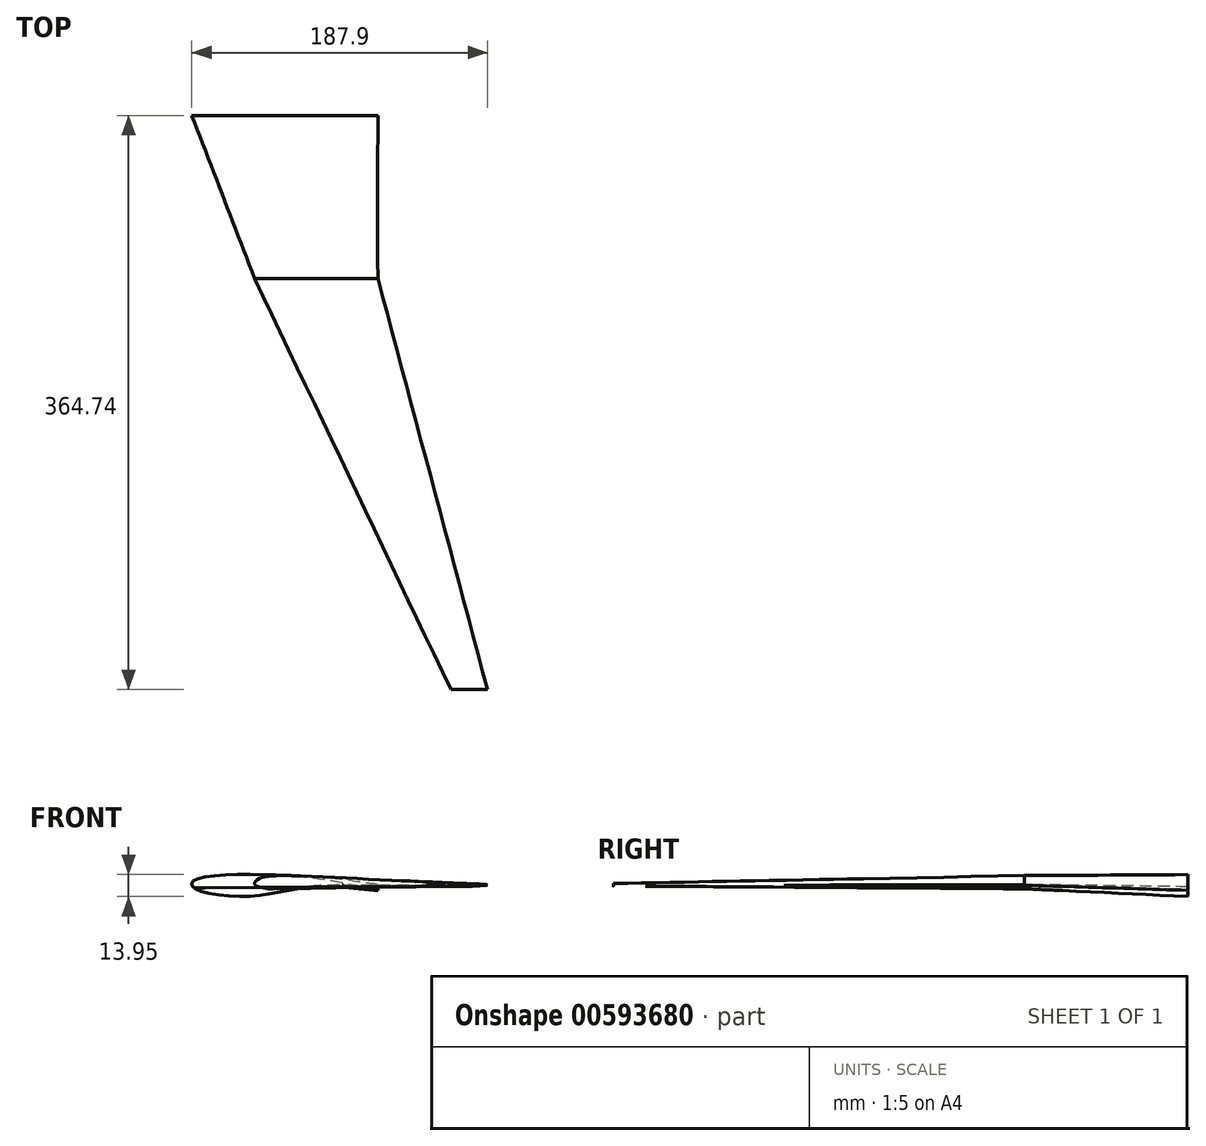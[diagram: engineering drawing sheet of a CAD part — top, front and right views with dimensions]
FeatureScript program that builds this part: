
annotation { "Feature Type Name" : "Feature", "Feature Type Description" : "" }
export const myFeature = defineFeature(function(context is Context, id is Id, definition is map)
    precondition{}
    {
        {
            var Q0;
            Q0=qCreatedBy(makeId("Front.planeOp"),FACE);
            cPlane(context, id + "F0", {"entities" : qUnion([Q0]), "cplaneType" : CPlaneType.OFFSET, "offset" : 129.03 * mm, "width" : 152.4 * mm, "height" : 152.4 * mm});
        }
        {
            var Q0;
            Q0=qCreatedBy(id+"F0.planeOp",FACE);
            var sketch = newSketch(context, id + "F1", { "sketchPlane" : qUnion([Q0])});
            skFitSpline(sketch, "E0", {"points": [v(59.9, 0) * mm, v(25.42, 4.56) * mm, v(1.57, 5.93) * mm, v(-15.04, 4.16) * mm, v(-18.32, 0.69) * mm, v(-14.73, -1.47) * mm, v(-7.44, -2.48) * mm, v(4.73, -1.57) * mm, v(25.42, 0) * mm, v(47.18, 0) * mm, v(59.9, 0) * mm]});
            skSolve(sketch);
        }
        {
            var Q0;
            Q0=qCreatedBy(makeId("Front.planeOp"),FACE);
            cPlane(context, id + "F2", {"entities" : qUnion([Q0]), "cplaneType" : CPlaneType.OFFSET, "offset" : 25.4 * mm, "width" : 152.4 * mm, "height" : 152.4 * mm});
        }
        {
            var Q0;
            Q0=qCreatedBy(id+"F2.planeOp",FACE);
            var sketch = newSketch(context, id + "F3", { "sketchPlane" : qUnion([Q0])});
            skFitSpline(sketch, "E1", {"points": [v(59.96, -3.36) * mm, v(25.15, 3.2) * mm, v(-14.76, 6.49) * mm, v(-55.04, 3.75) * mm, v(-58.32, 0.28) * mm, v(-55.04, -3) * mm, v(-24.6, -7.37) * mm, v(5.1, -3.17) * mm, v(25.34, -1.17) * mm, v(47.02, -2.26) * mm, v(59.96, -3.36) * mm]});
            skSolve(sketch);
        }
        {
            var Q0;
            Q0=qCreatedBy(id+"F0.planeOp",FACE);
            cPlane(context, id + "F4", {"entities" : qUnion([Q0]), "cplaneType" : CPlaneType.OFFSET, "offset" : 261.1 * mm, "width" : 152.4 * mm, "height" : 152.4 * mm});
        }
        {
            var Q0;
            Q0=qCreatedBy(id+"F4.planeOp",FACE);
            var sketch = newSketch(context, id + "F5", { "sketchPlane" : qUnion([Q0])});
            skFitSpline(sketch, "E2", {"points": [v(129.58, 0) * mm, v(120.15, 0.7) * mm, v(107.58, 0.61) * mm, v(106.28, 0) * mm, v(107.81, -0.61) * mm, v(120.3, -0.69) * mm, v(129.58, 0) * mm]});
            skSolve(sketch);
        }
        {
            var Q0;
            Q0=makeQuery(id+"F3.imprint","IMPRINT",FACE,{"disambiguationData":[TD([[makeQuery(id+"F3.imprint","IMPRINT",EDGE,{"derivedFrom":sQuery(id+"F3.wireOp",EDGE,"E1")}),1.0]])]});
            var Q1;
            Q1=makeQuery(id+"F1.imprint","IMPRINT",FACE,{"disambiguationData":[TD([[makeQuery(id+"F1.imprint","IMPRINT",EDGE,{"derivedFrom":sQuery(id+"F1.wireOp",EDGE,"E0")}),1.0]])]});
            loft(context, id + "F6", {"sheetProfilesArray" : [{ "sheetProfileEntities" : qUnion([Q0]) }, { "sheetProfileEntities" : qUnion([Q1]) }]});
        }
        {
            var Q1;
            Q1=makeQuery(id+"F5.imprint","IMPRINT",FACE,{"disambiguationData":[TD([[makeQuery(id+"F5.imprint","IMPRINT",EDGE,{"derivedFrom":sQuery(id+"F5.wireOp",EDGE,"E2")}),1.0]])]});
            var Q2;
            Q2=makeQuery(id+"F6.opLoft","CAP_FACE",FACE,{"disambiguationData":[OSD([makeQuery(id+"F1.imprint","IMPRINT",FACE,{"disambiguationData":[TD([[makeQuery(id+"F1.imprint","IMPRINT",EDGE,{"derivedFrom":sQuery(id+"F1.wireOp",EDGE,"E0")}),1.0]])]})])],"isStart":true});
            var Q3;
            Q3=sQuery(id+"F5.wireOp",VERTEX,"E2.2.internal");
            loft(context, id + "F7", {"operationType" : NewBodyOperationType.ADD, "sheetProfilesArray" : [{ "sheetProfileEntities" : qUnion([Q1]) }, { "sheetProfileEntities" : qUnion([Q2]) }], "connections" : [{ "connectionEntities" : qUnion([Q3]), "connectionEdgeQueries" : qUnion([]), "connectionEdgeParameters" : [] }]});
        }
    });
